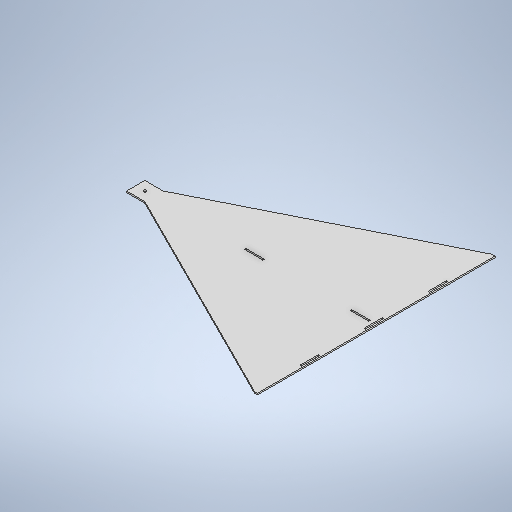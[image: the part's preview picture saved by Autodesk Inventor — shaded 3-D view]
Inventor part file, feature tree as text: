
AUTODESK INVENTOR PART (.ipt)
format: ipt  version: 2025.2 (Build 292293000, 293)  size: 324,608 bytes
history: native  units: mm
features: extrude x10, sketch x10
ambient origin geometry x8: Origin, YZ Plane, XZ Plane, XY Plane, X Axis, Y Axis, Z Axis, Center Point
bodies: Solid1 (feature_tree)
feature tree (20):
  extrude  "Extrusion1"  Depth=520.0mm
  extrude  "Extrusion2"  Depth=3.175mm
  extrude  "Extrusion3"  Depth=3.175mm TaperAngle=0.0deg
  extrude  "Extrusion4"  Depth=3.175mm TaperAngle=0.0deg
  extrude  "Extrusion5"  Depth=3.175mm TaperAngle=0.0deg
  extrude  "Extrusion6"  Depth=3.2mm
  extrude  "Extrusion7"  Depth=40.0mm
  extrude  "Extrusion8"  Depth=10.0mm TaperAngle=0.0deg
  extrude  "Extrusion9"  Depth=40.0mm
  extrude  "Extrusion10"  Depth=40.0mm
  sketch  "Sketch1"  dims[d1=260.0mm d2=520.0mm]
  sketch  "Sketch2"  dims[d3=3.175mm d4=0.0mm d6=6.35mm]
  sketch  "Sketch3"  dims[d7=3.175mm d8=0.0mm d9=3.175mm d10=0.0mm]
  sketch  "Sketch4"  dims[d11=40.0mm d12=3.175mm d13=0.0mm]
  sketch  "Sketch5"  dims[d15=6.35mm d16=3.175mm d17=0.0mm]
  sketch  "Sketch6"  dims[d18=3.175mm d19=0.0mm d23=3.2mm]
  sketch  "Sketch8"  dims[d24=3.2mm d27=40.0mm]
  sketch  "Sketch9"  dims[d28=10.0mm d29=0.0mm d31=10.0mm d32=0.0mm]
  sketch  "Sketch10"  dims[d38=40.0mm d39=40.0mm]
  sketch  "Sketch11"  dims[d40=10.0mm d41=0.0mm d44=40.0mm d45=10.0mm d46=0.0mm]
